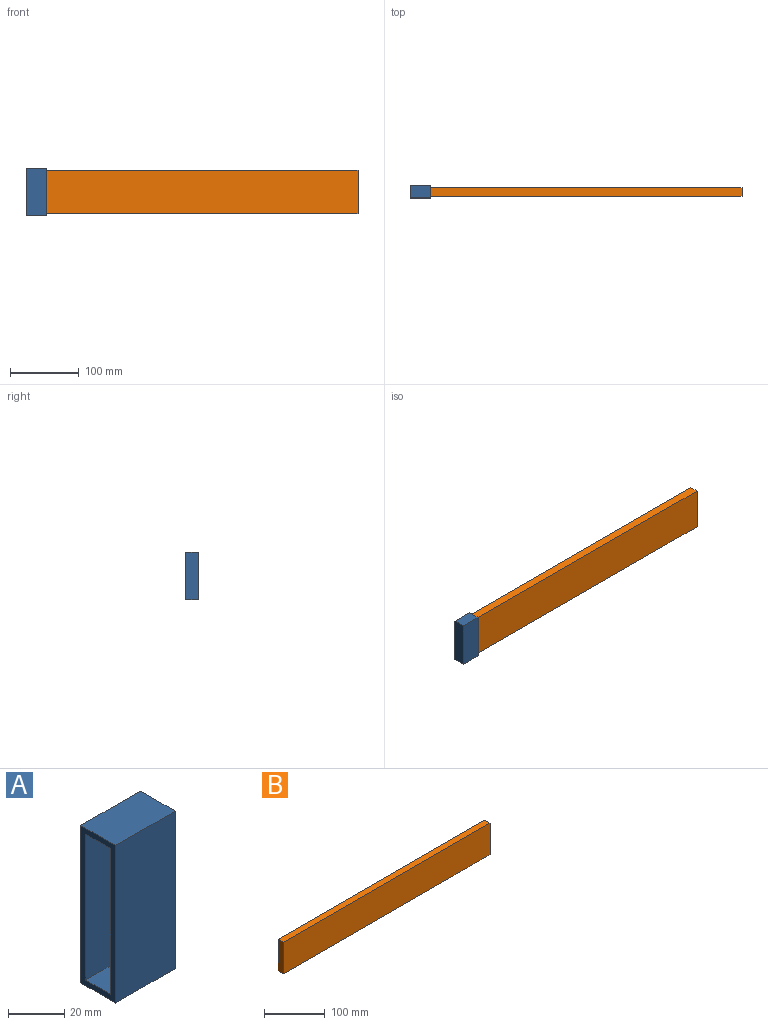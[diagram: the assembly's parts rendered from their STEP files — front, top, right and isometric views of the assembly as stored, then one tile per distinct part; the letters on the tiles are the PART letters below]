
ASSEMBLY  parts=2 mates=1
PART A: 11 faces, bbox 30x17.5x68.5 mm
  f0: plane 68.5x17.5mm, normal (-1,0,0), area 405mm2, adj f1,f2,f3,f4,f6,f7,f8,f9
  f1: plane 68.5x30mm, normal (0,-1,0), area 2055mm2, adj f0,f2,f4,f5
  f2: plane 30x17.5mm, normal (0,0,-1), area 525mm2, adj f0,f1,f3,f5
  f3: plane 68.5x30mm, normal (0,1,0), area 2055mm2, adj f0,f2,f4,f5
  f4: plane 30x17.5mm, normal (0,0,1), area 525mm2, adj f0,f1,f3,f5
  f5: plane 68.5x17.5mm, normal (1,0,0), area 1198.8mm2, adj f1,f2,f3,f4
  f6: plane 63.5x27.5mm, normal (0,1,0), area 1746.2mm2, adj f0,f7,f9,f10
  f7: plane 27.5x12.5mm, normal (0,0,1), area 343.8mm2, adj f0,f6,f8,f10
  f8: plane 63.5x27.5mm, normal (0,-1,0), area 1746.2mm2, adj f0,f7,f9,f10
  f9: plane 27.5x12.5mm, normal (0,0,-1), area 343.8mm2, adj f0,f6,f8,f10
  f10: plane 63.5x12.5mm, normal (-1,0,0), area 793.8mm2, adj f6,f7,f8,f9
PART B: 6 faces, bbox 480x12.5x63.5 mm
  f0: plane 480x63.5mm, normal (0,-1,0), area 30480mm2, adj f1,f3,f4,f5
  f1: plane 480x12.5mm, normal (0,0,-1), area 6000mm2, adj f0,f2,f4,f5
  f2: plane 480x63.5mm, normal (0,1,0), area 30480mm2, adj f1,f3,f4,f5
  f3: plane 480x12.5mm, normal (0,0,1), area 6000mm2, adj f0,f2,f4,f5
  f4: plane 63.5x12.5mm, normal (1,0,0), area 793.8mm2, adj f0,f1,f2,f3
  f5: plane 63.5x12.5mm, normal (-1,0,0), area 793.8mm2, adj f0,f1,f2,f3
PLACE A rot(axis=(0,1,0),180deg) t=(79.7,0,0)mm
PLACE B t=(52.2,0,0)mm
MATE fastened A.f10 <-> B.f5  axis (1,0,0) through (52.2,0,0)mm
